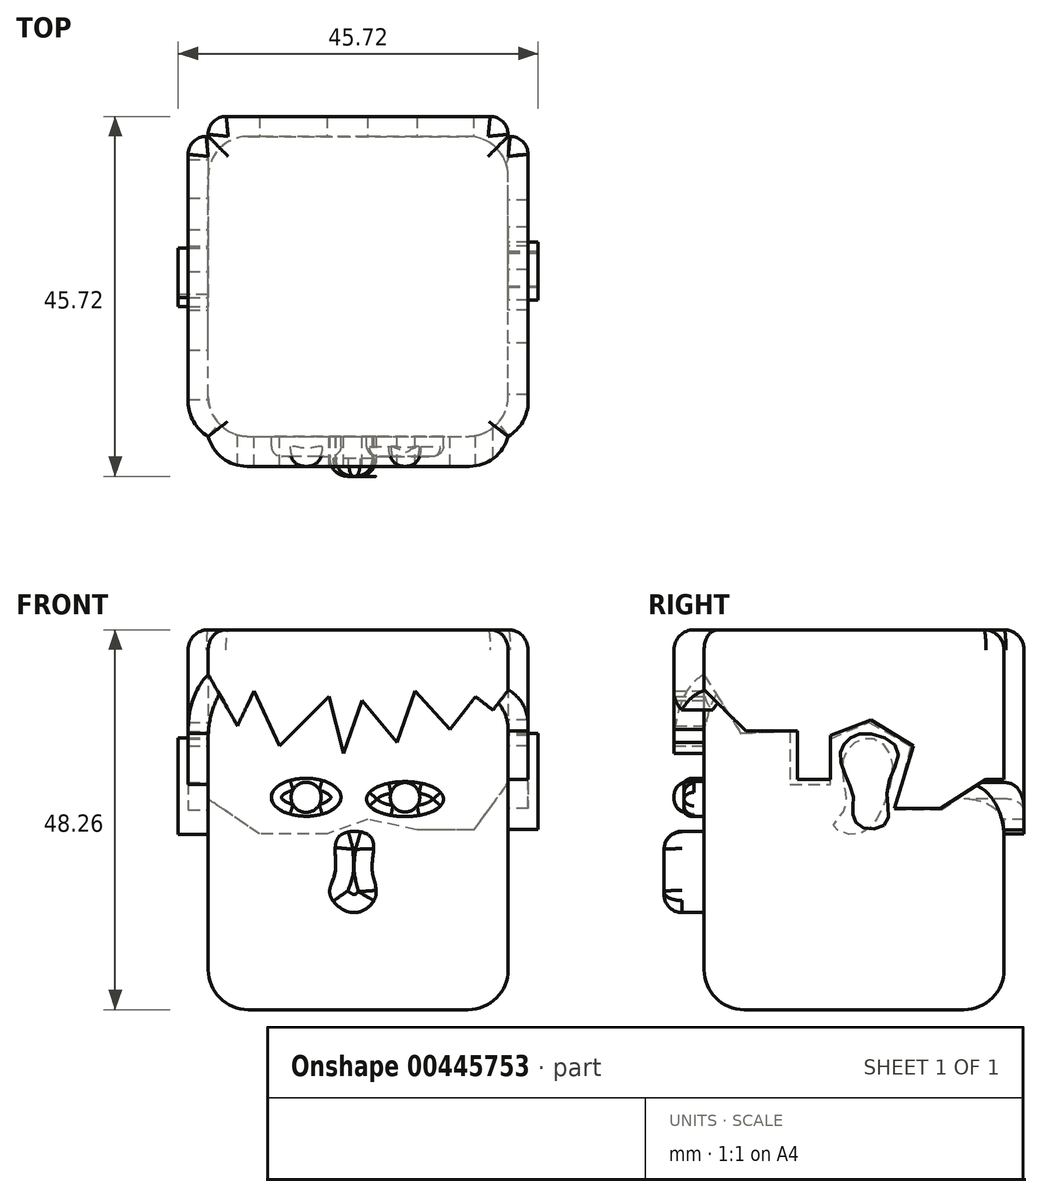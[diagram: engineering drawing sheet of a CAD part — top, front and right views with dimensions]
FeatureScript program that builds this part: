
annotation { "Feature Type Name" : "Feature", "Feature Type Description" : "" }
export const myFeature = defineFeature(function(context is Context, id is Id, definition is map)
    precondition{}
    {
        {
            var Q0;
            Q0=qCreatedBy(makeId("Top.planeOp"),FACE);
            var sketch = newSketch(context, id + "F0", { "sketchPlane" : qUnion([Q0])});
            skLineSegment(sketch, "E0.bottom", {"start": v(0, 0) * mm, "end": v(38.1, 0) * mm});
            skLineSegment(sketch, "E0.top", {"start": v(0, 38.1) * mm, "end": v(38.1, 38.1) * mm});
            skLineSegment(sketch, "E0.left", {"start": v(0, 0) * mm, "end": v(0, 38.1) * mm});
            skLineSegment(sketch, "E0.right", {"start": v(38.1, 0) * mm, "end": v(38.1, 38.1) * mm});
            skSolve(sketch);
        }
        {
            var Q0;
            Q0=makeQuery(id+"F0.imprint","IMPRINT",FACE,{"disambiguationData":[TD([[makeQuery(id+"F0.imprint","IMPRINT",EDGE,{"derivedFrom":sQuery(id+"F0.wireOp",EDGE,"E0.bottom")}),1.0]])]});
            extrude(context, id + "F1", {"entities" : qUnion([Q0]), "depth" : 45.72 * mm});
        }
        {
            var Q0;
            Q0=makeQuery(id+"F1.opExtrude","SWEPT_FACE",FACE,{"disambiguationData":[OSD([sQuery(id+"F0.wireOp",EDGE,"E0.bottom")])]});
            var sketch = newSketch(context, id + "F2", { "sketchPlane" : qUnion([Q0])});
            skLineSegment(sketch, "E1", {"start": v(0, 42.56) * mm, "end": v(3.72, 36.05) * mm});
            skLineSegment(sketch, "E2", {"start": v(3.72, 36.05) * mm, "end": v(5.81, 40.47) * mm});
            skLineSegment(sketch, "E3", {"start": v(5.81, 40.47) * mm, "end": v(9.07, 33.5) * mm});
            skLineSegment(sketch, "E4", {"start": v(9.07, 33.5) * mm, "end": v(15.35, 39.77) * mm});
            skLineSegment(sketch, "E5", {"start": v(15.35, 39.77) * mm, "end": v(17.21, 32.56) * mm});
            skLineSegment(sketch, "E6", {"start": v(17.21, 32.56) * mm, "end": v(19.54, 39.3) * mm});
            skLineSegment(sketch, "E7", {"start": v(19.54, 39.3) * mm, "end": v(23.96, 33.96) * mm});
            skLineSegment(sketch, "E8", {"start": v(23.96, 33.96) * mm, "end": v(26.28, 40.47) * mm});
            skLineSegment(sketch, "E9", {"start": v(26.28, 40.47) * mm, "end": v(30.7, 35.59) * mm});
            skLineSegment(sketch, "E10", {"start": v(30.7, 35.59) * mm, "end": v(33.96, 39.77) * mm});
            skLineSegment(sketch, "E11", {"start": v(33.96, 39.77) * mm, "end": v(36.16, 38.06) * mm});
            skLineSegment(sketch, "E12", {"start": v(36.16, 38.06) * mm, "end": v(38.1, 40.55) * mm});
            skSolve(sketch);
        }
        {
            var Q0;
            Q0=makeQuery(id+"F1.opExtrude","SWEPT_FACE",FACE,{"disambiguationData":[OSD([sQuery(id+"F0.wireOp",EDGE,"E0.right")])]});
            var sketch = newSketch(context, id + "F3", { "sketchPlane" : qUnion([Q0])});
            skLineSegment(sketch, "E13", {"start": v(0, 40.65) * mm, "end": v(5.3, 35.4) * mm});
            skLineSegment(sketch, "E14", {"start": v(5.3, 35.4) * mm, "end": v(11.87, 35.4) * mm});
            skLineSegment(sketch, "E15", {"start": v(11.87, 35.4) * mm, "end": v(11.87, 29.26) * mm});
            skLineSegment(sketch, "E16", {"start": v(11.87, 29.26) * mm, "end": v(16.04, 29.26) * mm});
            skLineSegment(sketch, "E17", {"start": v(16.04, 29.26) * mm, "end": v(16.04, 34.83) * mm});
            skLineSegment(sketch, "E18", {"start": v(16.04, 34.83) * mm, "end": v(21.17, 36.82) * mm});
            skLineSegment(sketch, "E19", {"start": v(21.17, 36.82) * mm, "end": v(26.6, 33.47) * mm});
            skLineSegment(sketch, "E20", {"start": v(26.6, 33.47) * mm, "end": v(24.19, 25.58) * mm});
            skLineSegment(sketch, "E21", {"start": v(24.19, 25.58) * mm, "end": v(30, 25.58) * mm});
            skLineSegment(sketch, "E22", {"start": v(30, 25.58) * mm, "end": v(35.82, 29.26) * mm});
            skLineSegment(sketch, "E23", {"start": v(35.82, 29.26) * mm, "end": v(38.1, 29.26) * mm});
            skSolve(sketch);
        }
        {
            var Q0;
            Q0=makeQuery(id+"F1.opExtrude","SWEPT_FACE",FACE,{"disambiguationData":[OSD([sQuery(id+"F0.wireOp",EDGE,"E0.top")])]});
            var sketch = newSketch(context, id + "F4", { "sketchPlane" : qUnion([Q0])});
            skLineSegment(sketch, "E24", {"start": v(-38.1, 28.84) * mm, "end": v(-33.73, 22.86) * mm});
            skPoint(sketch, "E24.endSnap0", {"position": v(-38.1, 22.86) * mm});
            skLineSegment(sketch, "E25", {"start": v(-33.73, 22.86) * mm, "end": v(-26.51, 22.86) * mm});
            skLineSegment(sketch, "E26", {"start": v(-26.51, 22.86) * mm, "end": v(-20.24, 24.19) * mm});
            skLineSegment(sketch, "E27", {"start": v(-20.24, 24.19) * mm, "end": v(-15.12, 22.33) * mm});
            skLineSegment(sketch, "E28", {"start": v(-15.12, 22.33) * mm, "end": v(-6.51, 22.33) * mm});
            skLineSegment(sketch, "E29", {"start": v(-6.51, 22.33) * mm, "end": v(0, 26.75) * mm});
            skSolve(sketch);
        }
        {
            var Q0;
            Q0=makeQuery(id+"F1.opExtrude","SWEPT_FACE",FACE,{"disambiguationData":[OSD([sQuery(id+"F0.wireOp",EDGE,"E0.left")])]});
            var sketch = newSketch(context, id + "F5", { "sketchPlane" : qUnion([Q0])});
            skLineSegment(sketch, "E30", {"start": v(0, 42.54) * mm, "end": v(-4.65, 35.12) * mm});
            skLineSegment(sketch, "E31", {"start": v(-4.65, 35.12) * mm, "end": v(-10.93, 35.35) * mm});
            skLineSegment(sketch, "E32", {"start": v(-10.93, 35.35) * mm, "end": v(-10.93, 28.6) * mm});
            skLineSegment(sketch, "E33", {"start": v(-10.93, 28.6) * mm, "end": v(-16.05, 28.6) * mm});
            skLineSegment(sketch, "E34", {"start": v(-16.05, 28.6) * mm, "end": v(-16.05, 34.42) * mm});
            skLineSegment(sketch, "E35", {"start": v(-16.05, 34.42) * mm, "end": v(-20.93, 36.52) * mm});
            skLineSegment(sketch, "E36", {"start": v(-20.93, 36.52) * mm, "end": v(-26.28, 33.5) * mm});
            skLineSegment(sketch, "E37", {"start": v(-26.28, 33.5) * mm, "end": v(-24.19, 25.35) * mm});
            skLineSegment(sketch, "E38", {"start": v(-35.12, 28.84) * mm, "end": v(-38.1, 28.84) * mm});
            skLineSegment(sketch, "E39", {"start": v(-35.12, 28.84) * mm, "end": v(-30.24, 25.35) * mm});
            skLineSegment(sketch, "E40", {"start": v(-30.24, 25.35) * mm, "end": v(-24.19, 25.35) * mm});
            skSolve(sketch);
        }
        {
            var Q0;
            {var subQ0=sQuery(id+"F2.wireOp",EDGE,"E1");Q0=makeQuery(id+"F2.imprint","IMPRINT",FACE,{"disambiguationData":[TD([[makeQuery(id+"F2.imprint","IMPRINT",EDGE,{"derivedFrom":subQ0}),1.0]])]});}
            extrude(context, id + "F6", {"entities" : qUnion([Q0]), "operationType" : NewBodyOperationType.ADD, "depth" : 3.8 * mm});
        }
        {
            var Q0;
            {var subQ1=sQuery(id+"F5.wireOp",EDGE,"E30");Q0=makeQuery(id+"F5.imprint","IMPRINT",FACE,{"disambiguationData":[TD([[makeQuery(id+"F5.imprint","IMPRINT",EDGE,{"derivedFrom":subQ1}),-1.0]])]});}
            extrude(context, id + "F7", {"entities" : qUnion([Q0]), "operationType" : NewBodyOperationType.ADD, "depth" : 2.54 * mm});
        }
        {
            var Q0;
            {var subQ0=sQuery(id+"F3.wireOp",EDGE,"E13");Q0=makeQuery(id+"F3.imprint","IMPRINT",FACE,{"disambiguationData":[TD([[makeQuery(id+"F3.imprint","IMPRINT",EDGE,{"derivedFrom":subQ0}),1.0]])]});}
            extrude(context, id + "F8", {"entities" : qUnion([Q0]), "operationType" : NewBodyOperationType.ADD, "depth" : 2.54 * mm});
        }
        {
            var Q0;
            {var subQ0=sQuery(id+"F4.wireOp",EDGE,"E24");Q0=makeQuery(id+"F4.imprint","IMPRINT",FACE,{"disambiguationData":[TD([[makeQuery(id+"F4.imprint","IMPRINT",EDGE,{"derivedFrom":subQ0}),1.0]])]});}
            extrude(context, id + "F9", {"entities" : qUnion([Q0]), "operationType" : NewBodyOperationType.ADD, "depth" : 2.54 * mm});
        }
        {
            var Q0;
            {var subQ0=sQuery(id+"F0.wireOp",EDGE,"E0.top");var subQ1=sQuery(id+"F0.wireOp",EDGE,"E0.right");var subQ2=sQuery(id+"F0.wireOp",EDGE,"E0.left");var subQ3=sQuery(id+"F0.wireOp",EDGE,"E0.bottom");Q0=makeQuery(id+"F9.boolean.opBoolean","MERGE",FACE,{"derivedFrom":[makeQuery(id+"F8.boolean.opBoolean","MERGE",FACE,{"derivedFrom":[makeQuery(id+"F7.boolean.opBoolean","MERGE",FACE,{"derivedFrom":[makeQuery(id+"F6.boolean.opBoolean","MERGE",FACE,{"derivedFrom":[makeQuery(id+"F1.opExtrude","CAP_FACE",FACE,{"disambiguationData":[OSD([subQ3,subQ0,subQ2,subQ1])],"isStart":false}),makeQuery(id+"F6.opExtrude","SWEPT_FACE",FACE,{"disambiguationData":[OSD([subQ3])]})]}),makeQuery(id+"F7.opExtrude","SWEPT_FACE",FACE,{"disambiguationData":[OSD([subQ2])]})]}),makeQuery(id+"F8.opExtrude","SWEPT_FACE",FACE,{"disambiguationData":[OSD([subQ1])]})]}),makeQuery(id+"F9.opExtrude","SWEPT_FACE",FACE,{"disambiguationData":[OSD([subQ0])]})]});}
            extrude(context, id + "F10", {"entities" : qUnion([Q0]), "operationType" : NewBodyOperationType.ADD, "depth" : 2.54 * mm});
        }
        {
            var Q0;
            Q0=makeQuery(id+"F1.opExtrude","SWEPT_EDGE",EDGE,{"disambiguationData":[OSD([sQuery(id+"F0.wireOp",EDGE,"E0.bottom"),sQuery(id+"F0.wireOp",EDGE,"E0.left")])]});
            fillet(context, id + "F11", {"entities" : qUnion([Q0]), "radius" : 5.08 * mm, "tangentPropagation" : true, "allowEdgeOverflow" : false});
        }
        {
            var Q0;
            Q0=makeQuery(id+"F1.opExtrude","SWEPT_EDGE",EDGE,{"disambiguationData":[OSD([sQuery(id+"F0.wireOp",EDGE,"E0.bottom"),sQuery(id+"F0.wireOp",EDGE,"E0.right")])]});
            fillet(context, id + "F12", {"entities" : qUnion([Q0]), "radius" : 5.08 * mm, "tangentPropagation" : true, "allowEdgeOverflow" : false});
        }
        {
            var Q0;
            Q0=makeQuery(id+"F1.opExtrude","SWEPT_EDGE",EDGE,{"disambiguationData":[OSD([sQuery(id+"F0.wireOp",EDGE,"E0.top"),sQuery(id+"F0.wireOp",EDGE,"E0.right")])]});
            var Q1;
            Q1=makeQuery(id+"F1.opExtrude","SWEPT_EDGE",EDGE,{"disambiguationData":[OSD([sQuery(id+"F0.wireOp",EDGE,"E0.top"),sQuery(id+"F0.wireOp",EDGE,"E0.left")])]});
            fillet(context, id + "F13", {"entities" : qUnion([Q0, Q1]), "radius" : 5.08 * mm, "tangentPropagation" : true, "allowEdgeOverflow" : false});
        }
        {
            var Q0;
            {var subQ0=sQuery(id+"F0.wireOp",EDGE,"E0.left");var subQ1=sQuery(id+"F0.wireOp",EDGE,"E0.top");Q0=makeQuery(id+"F10.boolean.opBoolean","MERGE",EDGE,{"derivedFrom":[makeQuery(id+"F9.opExtrude","CAP_EDGE",EDGE,{"disambiguationData":[OSD([subQ1,subQ0])],"isStart":false}),makeQuery(id+"F10.opExtrude","SWEPT_EDGE",EDGE,{"disambiguationData":[OSD([subQ1,subQ0]),TDD([makeQuery(id+"F9.opExtrude","CAP_VERTEX",VERTEX,{"disambiguationData":[OSD([subQ1,subQ0])],"isStart":false})])]})]});}
            var Q1;
            {var subQ0=sQuery(id+"F0.wireOp",EDGE,"E0.left");var subQ1=sQuery(id+"F0.wireOp",EDGE,"E0.top");Q1=makeQuery(id+"F10.boolean.opBoolean","MERGE",EDGE,{"derivedFrom":[makeQuery(id+"F7.opExtrude","CAP_EDGE",EDGE,{"disambiguationData":[OSD([subQ1,subQ0])],"isStart":false}),makeQuery(id+"F10.opExtrude","SWEPT_EDGE",EDGE,{"disambiguationData":[OSD([subQ1,subQ0]),TDD([makeQuery(id+"F7.opExtrude","CAP_VERTEX",VERTEX,{"disambiguationData":[OSD([subQ1,subQ0])],"isStart":false})])]})]});}
            fillet(context, id + "F14", {"entities" : qUnion([Q0, Q1]), "radius" : 2.3 * mm, "tangentPropagation" : true, "allowEdgeOverflow" : false});
        }
        {
            var Q0;
            {var subQ0=sQuery(id+"F0.wireOp",EDGE,"E0.right");var subQ1=sQuery(id+"F0.wireOp",EDGE,"E0.top");Q0=makeQuery(id+"F10.boolean.opBoolean","MERGE",EDGE,{"derivedFrom":[makeQuery(id+"F8.opExtrude","CAP_EDGE",EDGE,{"disambiguationData":[OSD([subQ1,subQ0])],"isStart":false}),makeQuery(id+"F10.opExtrude","SWEPT_EDGE",EDGE,{"disambiguationData":[OSD([subQ1,subQ0]),TDD([makeQuery(id+"F8.opExtrude","CAP_VERTEX",VERTEX,{"disambiguationData":[OSD([subQ1,subQ0])],"isStart":false})])]})]});}
            var Q1;
            {var subQ0=sQuery(id+"F0.wireOp",EDGE,"E0.right");var subQ1=sQuery(id+"F0.wireOp",EDGE,"E0.top");Q1=makeQuery(id+"F10.boolean.opBoolean","MERGE",EDGE,{"derivedFrom":[makeQuery(id+"F9.opExtrude","CAP_EDGE",EDGE,{"disambiguationData":[OSD([subQ1,subQ0])],"isStart":false}),makeQuery(id+"F10.opExtrude","SWEPT_EDGE",EDGE,{"disambiguationData":[OSD([subQ1,subQ0]),TDD([makeQuery(id+"F9.opExtrude","CAP_VERTEX",VERTEX,{"disambiguationData":[OSD([subQ1,subQ0])],"isStart":false})])]})]});}
            fillet(context, id + "F15", {"entities" : qUnion([Q0, Q1]), "radius" : 2.3 * mm, "tangentPropagation" : true, "allowEdgeOverflow" : false});
        }
        {
            var Q0;
            {var subQ0=sQuery(id+"F0.wireOp",EDGE,"E0.left");var subQ1=sQuery(id+"F0.wireOp",EDGE,"E0.bottom");Q0=makeQuery(id+"F10.boolean.opBoolean","MERGE",EDGE,{"derivedFrom":[makeQuery(id+"F7.opExtrude","CAP_EDGE",EDGE,{"disambiguationData":[OSD([subQ1,subQ0])],"isStart":false}),makeQuery(id+"F10.opExtrude","SWEPT_EDGE",EDGE,{"disambiguationData":[OSD([subQ1,subQ0]),TDD([makeQuery(id+"F7.opExtrude","CAP_VERTEX",VERTEX,{"disambiguationData":[OSD([subQ1,subQ0])],"isStart":false})])]})]});}
            var Q1;
            {var subQ0=sQuery(id+"F0.wireOp",EDGE,"E0.left");var subQ1=sQuery(id+"F0.wireOp",EDGE,"E0.bottom");Q1=makeQuery(id+"F10.boolean.opBoolean","MERGE",EDGE,{"derivedFrom":[makeQuery(id+"F6.opExtrude","CAP_EDGE",EDGE,{"disambiguationData":[OSD([subQ1,subQ0])],"isStart":false}),makeQuery(id+"F10.opExtrude","SWEPT_EDGE",EDGE,{"disambiguationData":[OSD([subQ1,subQ0]),TDD([makeQuery(id+"F6.opExtrude","CAP_VERTEX",VERTEX,{"disambiguationData":[OSD([subQ1,subQ0])],"isStart":false})])]})]});}
            fillet(context, id + "F16", {"entities" : qUnion([Q0, Q1]), "radius" : 5.08 * mm, "tangentPropagation" : true, "allowEdgeOverflow" : false});
        }
        {
            var Q0;
            {var subQ0=sQuery(id+"F0.wireOp",EDGE,"E0.right");var subQ1=sQuery(id+"F0.wireOp",EDGE,"E0.bottom");Q0=makeQuery(id+"F10.boolean.opBoolean","MERGE",EDGE,{"derivedFrom":[makeQuery(id+"F8.opExtrude","CAP_EDGE",EDGE,{"disambiguationData":[OSD([subQ1,subQ0])],"isStart":false}),makeQuery(id+"F10.opExtrude","SWEPT_EDGE",EDGE,{"disambiguationData":[OSD([subQ1,subQ0]),TDD([makeQuery(id+"F8.opExtrude","CAP_VERTEX",VERTEX,{"disambiguationData":[OSD([subQ1,subQ0])],"isStart":false})])]})]});}
            var Q1;
            {var subQ0=sQuery(id+"F0.wireOp",EDGE,"E0.right");var subQ1=sQuery(id+"F0.wireOp",EDGE,"E0.bottom");Q1=makeQuery(id+"F10.boolean.opBoolean","MERGE",EDGE,{"derivedFrom":[makeQuery(id+"F6.opExtrude","CAP_EDGE",EDGE,{"disambiguationData":[OSD([subQ1,subQ0])],"isStart":false}),makeQuery(id+"F10.opExtrude","SWEPT_EDGE",EDGE,{"disambiguationData":[OSD([subQ1,subQ0]),TDD([makeQuery(id+"F6.opExtrude","CAP_VERTEX",VERTEX,{"disambiguationData":[OSD([subQ1,subQ0])],"isStart":false})])]})]});}
            fillet(context, id + "F17", {"entities" : qUnion([Q0, Q1]), "radius" : 5.08 * mm, "tangentPropagation" : true, "allowEdgeOverflow" : false});
        }
        {
            var Q0;
            {var subQ0=sQuery(id+"F0.wireOp",EDGE,"E0.left");var subQ1=sQuery(id+"F0.wireOp",EDGE,"E0.top");var subQ2=sQuery(id+"F0.wireOp",EDGE,"E0.bottom");Q0=makeQuery(id+"F10.boolean.opBoolean","MERGE",FACE,{"derivedFrom":[makeQuery(id+"F9.boolean.opBoolean","MERGE",FACE,{"derivedFrom":[makeQuery(id+"F7.boolean.opBoolean","SPLIT",FACE,{"disambiguationData":[TD([makeQuery(id+"F1.opExtrude","SWEPT_FACE",FACE,{"disambiguationData":[OSD([subQ1])]})])],"derivedFrom":makeQuery(id+"F6.boolean.opBoolean","MERGE",FACE,{"derivedFrom":[makeQuery(id+"F1.opExtrude","SWEPT_FACE",FACE,{"disambiguationData":[OSD([subQ0])]}),makeQuery(id+"F6.opExtrude","SWEPT_FACE",FACE,{"disambiguationData":[OSD([subQ2,subQ0])]})]})}),makeQuery(id+"F9.opExtrude","SWEPT_FACE",FACE,{"disambiguationData":[OSD([subQ1,subQ0])]})]}),makeQuery(id+"F10.opExtrude","SWEPT_FACE",FACE,{"disambiguationData":[OSD([subQ1,subQ0])]})]});}
            var sketch = newSketch(context, id + "F18", { "sketchPlane" : qUnion([Q0])});
            skFitSpline(sketch, "E41", {"points": [v(-17.75, 28.97) * mm, v(-18.17, 32.9) * mm, v(-21.08, 34.53) * mm, v(-23.74, 32.05) * mm, v(-22.62, 25.54) * mm, v(-19.46, 22.3) * mm, v(-16.46, 23.32) * mm, v(-17.83, 25.29) * mm, v(-17.75, 28.97) * mm]});
            skSolve(sketch);
        }
        {
            var Q0;
            Q0=makeQuery(id+"F18.imprint","IMPRINT",FACE,{"disambiguationData":[TD([[makeQuery(id+"F18.imprint","IMPRINT",EDGE,{"derivedFrom":sQuery(id+"F18.wireOp",EDGE,"E41")}),1.0]])]});
            extrude(context, id + "F19", {"entities" : qUnion([Q0]), "operationType" : NewBodyOperationType.ADD, "depth" : 3.8 * mm});
        }
        {
            var Q0;
            {var subQ0=sQuery(id+"F0.wireOp",EDGE,"E0.left");var subQ1=sQuery(id+"F0.wireOp",EDGE,"E0.bottom");Q0=makeQuery(id+"F11.opFillet","SPLIT",FACE,{"disambiguationData":[OD(0.0)],"derivedFrom":makeQuery(id+"F10.boolean.opBoolean","MERGE",FACE,{"derivedFrom":[makeQuery(id+"F7.boolean.opBoolean","MERGE",FACE,{"derivedFrom":[makeQuery(id+"F1.opExtrude","SWEPT_FACE",FACE,{"disambiguationData":[OSD([subQ1])]}),makeQuery(id+"F7.opExtrude","SWEPT_FACE",FACE,{"disambiguationData":[OSD([subQ1,subQ0])]})]}),makeQuery(id+"F10.opExtrude","SWEPT_FACE",FACE,{"disambiguationData":[OSD([subQ1,subQ0]),TDD([makeQuery(id+"F7.opExtrude","SWEPT_EDGE",EDGE,{"disambiguationData":[OSD([subQ1,subQ0])]})])]})]})});}
            var sketch = newSketch(context, id + "F20", { "sketchPlane" : qUnion([Q0])});
            skEllipse(sketch, "E42", {"center": v(12.44, 26.98) * mm, "majorRadius": 4.42 * mm, "minorRadius": 2.41 * mm, "majorAxis": v(1, 0)});
            skEllipse(sketch, "E43", {"center": v(25, 26.75) * mm, "majorRadius": 4.88 * mm, "minorRadius": 2.22 * mm, "majorAxis": v(1, 0)});
            skSolve(sketch);
        }
        {
            var Q0;
            Q0=makeQuery(id+"F20.imprint","IMPRINT",FACE,{"disambiguationData":[TD([[makeQuery(id+"F20.imprint","IMPRINT",EDGE,{"derivedFrom":sQuery(id+"F20.wireOp",EDGE,"E43")}),1.0]])]});
            var Q1;
            Q1=makeQuery(id+"F20.imprint","IMPRINT",FACE,{"disambiguationData":[TD([[makeQuery(id+"F20.imprint","IMPRINT",EDGE,{"derivedFrom":sQuery(id+"F20.wireOp",EDGE,"E42")}),1.0]])]});
            var Q2;
            Q2=sQuery(id+"F20.wireOp",EDGE,"E43");
            var Q3;
            Q3=sQuery(id+"F20.wireOp",EDGE,"E42");
            extrude(context, id + "F21", {"entities" : qUnion([Q0, Q1]), "operationType" : NewBodyOperationType.ADD, "surfaceEntities" : qUnion([Q2, Q3]), "depth" : 2.54 * mm});
        }
        {
            var Q0;
            Q0=makeQuery(id+"F21.opExtrude","CAP_FACE",FACE,{"disambiguationData":[OSD([sQuery(id+"F20.wireOp",EDGE,"E42")])],"isStart":false});
            var sketch = newSketch(context, id + "F22", { "sketchPlane" : qUnion([Q0])});
            skCircle(sketch, "E44", {"center": v(12.44, 26.98) * mm, "radius": 1.92 * mm});
            skPoint(sketch, "E45.centerSnap0", {"position": v(16.86, 26.98) * mm});
            skCircle(sketch, "E46", {"center": v(25, 26.98) * mm, "radius": 1.88 * mm});
            skSolve(sketch);
        }
        {
            var Q0;
            Q0=makeQuery(id+"F22.imprint","IMPRINT",FACE,{"disambiguationData":[TD([[makeQuery(id+"F22.imprint","IMPRINT",EDGE,{"derivedFrom":sQuery(id+"F22.wireOp",EDGE,"E46")}),1.0]])]});
            var Q1;
            Q1=makeQuery(id+"F22.imprint","IMPRINT",FACE,{"disambiguationData":[TD([[makeQuery(id+"F22.imprint","IMPRINT",EDGE,{"derivedFrom":sQuery(id+"F22.wireOp",EDGE,"E44")}),1.0]])]});
            extrude(context, id + "F23", {"entities" : qUnion([Q0, Q1]), "operationType" : NewBodyOperationType.ADD, "depth" : 1.27 * mm});
        }
        {
            var Q0;
            Q0=makeQuery(id+"F23.opExtrude","CAP_EDGE",EDGE,{"disambiguationData":[OSD([sQuery(id+"F22.wireOp",EDGE,"E46")])],"isStart":false});
            var Q1;
            Q1=makeQuery(id+"F23.opExtrude","CAP_EDGE",EDGE,{"disambiguationData":[OSD([sQuery(id+"F22.wireOp",EDGE,"E44")])],"isStart":false});
            fillet(context, id + "F24", {"entities" : qUnion([Q0, Q1]), "radius" : 1.78 * mm, "tangentPropagation" : true, "allowEdgeOverflow" : false});
        }
        {
            var Q0;
            Q0=makeQuery(id+"F21.opExtrude","CAP_EDGE",EDGE,{"disambiguationData":[OSD([sQuery(id+"F20.wireOp",EDGE,"E43")])],"isStart":false});
            var Q1;
            Q1=makeQuery(id+"F21.opExtrude","CAP_EDGE",EDGE,{"disambiguationData":[OSD([sQuery(id+"F20.wireOp",EDGE,"E42")])],"isStart":false});
            fillet(context, id + "F25", {"entities" : qUnion([Q0, Q1]), "radius" : 1.27 * mm, "tangentPropagation" : true, "allowEdgeOverflow" : false});
        }
        {
            var Q0;
            Q0=makeQuery(id+"F1.opExtrude","CAP_FACE",FACE,{"disambiguationData":[OSD([sQuery(id+"F0.wireOp",EDGE,"E0.bottom"),sQuery(id+"F0.wireOp",EDGE,"E0.top"),sQuery(id+"F0.wireOp",EDGE,"E0.left"),sQuery(id+"F0.wireOp",EDGE,"E0.right")])],"isStart":true});
            fillet(context, id + "F26", {"entities" : qUnion([Q0]), "radius" : 5.08 * mm, "tangentPropagation" : true, "allowEdgeOverflow" : false});
        }
        {
            var Q0;
            Q0=makeQuery(id+"F10.opExtrude","CAP_FACE",FACE,{"disambiguationData":[OSD([sQuery(id+"F0.wireOp",EDGE,"E0.bottom"),sQuery(id+"F0.wireOp",EDGE,"E0.top"),sQuery(id+"F0.wireOp",EDGE,"E0.left"),sQuery(id+"F0.wireOp",EDGE,"E0.right")])],"isStart":false});
            fillet(context, id + "F27", {"entities" : qUnion([Q0]), "radius" : 2.54 * mm, "tangentPropagation" : true, "allowEdgeOverflow" : false});
        }
        {
            var Q0;
            {var subQ0=sQuery(id+"F0.wireOp",EDGE,"E0.left");var subQ1=sQuery(id+"F0.wireOp",EDGE,"E0.bottom");Q0=makeQuery(id+"F11.opFillet","SPLIT",FACE,{"disambiguationData":[OD(0.0)],"derivedFrom":makeQuery(id+"F10.boolean.opBoolean","MERGE",FACE,{"derivedFrom":[makeQuery(id+"F7.boolean.opBoolean","MERGE",FACE,{"derivedFrom":[makeQuery(id+"F1.opExtrude","SWEPT_FACE",FACE,{"disambiguationData":[OSD([subQ1])]}),makeQuery(id+"F7.opExtrude","SWEPT_FACE",FACE,{"disambiguationData":[OSD([subQ1,subQ0])]})]}),makeQuery(id+"F10.opExtrude","SWEPT_FACE",FACE,{"disambiguationData":[OSD([subQ1,subQ0]),TDD([makeQuery(id+"F7.opExtrude","SWEPT_EDGE",EDGE,{"disambiguationData":[OSD([subQ1,subQ0])]})])]})]})});}
            var sketch = newSketch(context, id + "F28", { "sketchPlane" : qUnion([Q0])});
            skPoint(sketch, "E47.0.internal.snap0", {"position": v(5.08, 22) * mm});
            skPoint(sketch, "E47.6.internal.snap0", {"position": v(5.08, 22) * mm});
            skFitSpline(sketch, "E47", {"points": [v(16.63, 22) * mm, v(16.16, 17.68) * mm, v(15.47, 14.65) * mm, v(18.5, 12.33) * mm, v(21.28, 14.42) * mm, v(20.82, 17.9) * mm, v(20.58, 22) * mm, v(16.63, 22) * mm]});
            skSolve(sketch);
        }
        {
            var Q0;
            Q0 = qSketchRegion(id + "F28", true);
            extrude(context, id + "F29", {"entities" : qUnion([Q0]), "operationType" : NewBodyOperationType.ADD, "depth" : 5.08 * mm});
        }
        {
            var Q0;
            Q0=makeQuery(id+"F29.opExtrude","CAP_EDGE",EDGE,{"disambiguationData":[OSD([sQuery(id+"F28.wireOp",EDGE,"E47")])],"isStart":false});
            fillet(context, id + "F30", {"entities" : qUnion([Q0]), "radius" : 2.3 * mm, "tangentPropagation" : true, "allowEdgeOverflow" : false});
        }
        {
            var Q0;
            {var subQ0=sQuery(id+"F0.wireOp",EDGE,"E0.right");var subQ1=sQuery(id+"F0.wireOp",EDGE,"E0.top");var subQ2=sQuery(id+"F0.wireOp",EDGE,"E0.bottom");Q0=makeQuery(id+"F13.opFillet","SPLIT",FACE,{"disambiguationData":[OD(0.0)],"derivedFrom":makeQuery(id+"F12.opFillet","SPLIT",FACE,{"disambiguationData":[OD(0.0)],"derivedFrom":makeQuery(id+"F10.boolean.opBoolean","MERGE",FACE,{"derivedFrom":[makeQuery(id+"F9.boolean.opBoolean","MERGE",FACE,{"derivedFrom":[makeQuery(id+"F6.boolean.opBoolean","MERGE",FACE,{"derivedFrom":[makeQuery(id+"F1.opExtrude","SWEPT_FACE",FACE,{"disambiguationData":[OSD([subQ0])]}),makeQuery(id+"F6.opExtrude","SWEPT_FACE",FACE,{"disambiguationData":[OSD([subQ2,subQ0])]})]}),makeQuery(id+"F9.opExtrude","SWEPT_FACE",FACE,{"disambiguationData":[OSD([subQ1,subQ0])]})]}),makeQuery(id+"F10.opExtrude","SWEPT_FACE",FACE,{"disambiguationData":[OSD([subQ2,subQ0]),TDD([makeQuery(id+"F6.boolean.opBoolean","MERGE",EDGE,{"derivedFrom":[makeQuery(id+"F1.opExtrude","CAP_EDGE",EDGE,{"disambiguationData":[OSD([subQ0])],"isStart":false}),makeQuery(id+"F6.opExtrude","SWEPT_EDGE",EDGE,{"disambiguationData":[OSD([subQ2,subQ0])]})]})])]}),makeQuery(id+"F10.opExtrude","SWEPT_FACE",FACE,{"disambiguationData":[OSD([subQ1,subQ0])]})]})})});}
            var sketch = newSketch(context, id + "F31", { "sketchPlane" : qUnion([Q0])});
            skFitSpline(sketch, "E48", {"points": [v(17.39, 31.38) * mm, v(17.91, 33.94) * mm, v(20.59, 35.1) * mm, v(24.6, 33) * mm, v(23.26, 28.12) * mm, v(23.26, 23.88) * mm, v(20.47, 23) * mm, v(18.9, 24.75) * mm, v(18.96, 27.13) * mm, v(17.39, 31.38) * mm]});
            skSolve(sketch);
        }
        {
            var Q0;
            Q0=makeQuery(id+"F31.imprint","IMPRINT",FACE,{"disambiguationData":[TD([[makeQuery(id+"F31.imprint","IMPRINT",EDGE,{"derivedFrom":sQuery(id+"F31.wireOp",EDGE,"E48")}),-1.0]])]});
            extrude(context, id + "F32", {"entities" : qUnion([Q0]), "operationType" : NewBodyOperationType.ADD, "depth" : 3.8 * mm});
        }
    });
